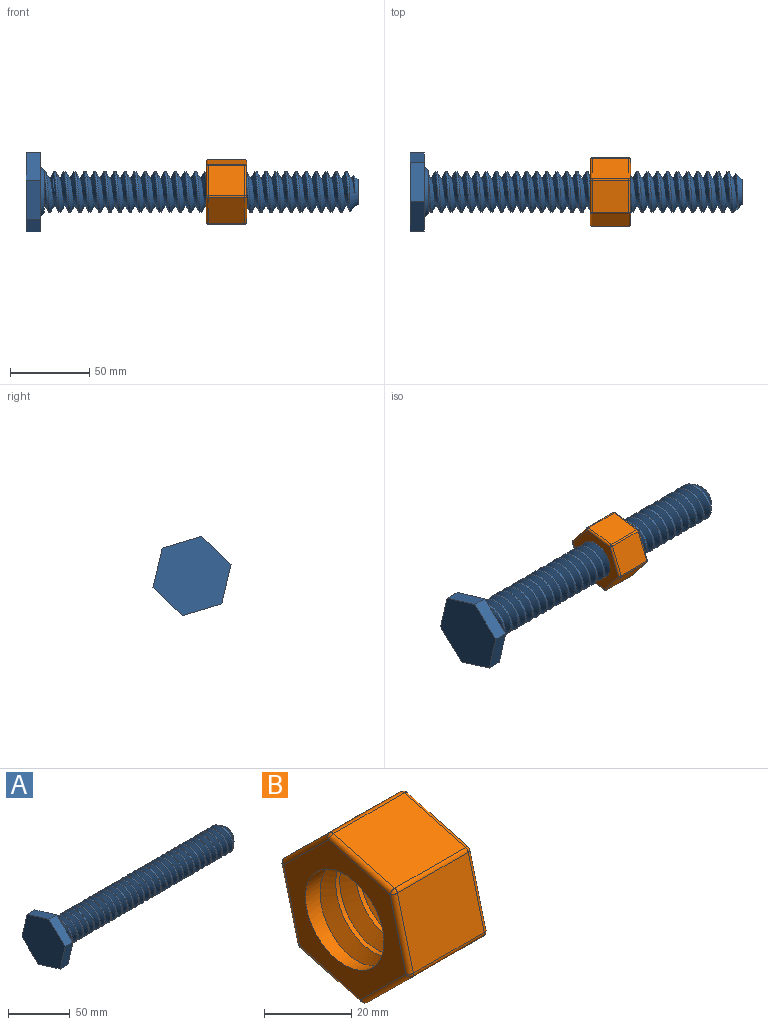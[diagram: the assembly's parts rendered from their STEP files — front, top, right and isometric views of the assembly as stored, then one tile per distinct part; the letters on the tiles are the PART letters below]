
ASSEMBLY  parts=2 mates=1
PART A: 16 faces, bbox 209.6x49.3x50.2 mm
  f0: plane 50.15x49.26mm, normal (1,0,0), area 936.9mm2, adj f1,f2,f3,f4,f5,f6,f15
  f1: plane 18.8x17.58mm, normal (0,-0.68,0.73), area 228.9mm2, adj f0,f2,f6,f7
  f2: plane 24.63x8.89mm, normal (0,0.29,0.96), area 228.9mm2, adj f0,f1,f3,f7
  f3: plane 25.08x8.89mm, normal (0,0.97,0.23), area 228.9mm2, adj f0,f2,f4,f7
  f4: plane 18.8x17.58mm, normal (0,0.68,-0.73), area 228.9mm2, adj f0,f3,f5,f7
  f5: plane 24.63x8.89mm, normal (0,-0.29,-0.96), area 228.9mm2, adj f0,f4,f6,f7
  f6: plane 25.08x8.89mm, normal (0,-0.97,-0.23), area 228.9mm2, adj f0,f1,f5,f7
  f7: plane 50.15x49.26mm, normal (-1,0,0), area 1721.8mm2, adj f1,f2,f3,f4,f5,f6
  f8: plane 26.53x26.53mm, normal (1,0,0), area 170.4mm2, adj f12,f13,f14,f15
  f9: plane 15.24x15.24mm, normal (1,0,0), area 182.4mm2, adj f10
  f10: cone r=7.62mm half-angle=45deg, axis (-1,0,0), area 325.5mm2, adj f9,f11,f12,f14
  f11: plane 4.4x3.22mm, normal (0,0,1), area 3mm2, adj f10,f12,f13
  f12: bspline ~201.51x29.33mm, area 10332.3mm2, adj f8,f10,f11,f13,f14
  f13: bspline ~198.33x29.33mm, area 10303.2mm2, adj f8,f11,f12,f14
  f14: cylinder r=12.7mm len=193.04mm, axis (-1,0,0), area 1188.4mm2, adj f8,f10,f12,f13
  f15: cone r=18.35mm half-angle=45deg, axis (-1,0,0), area 328.1mm2, adj f0,f8
PART B: 45 faces, bbox 31.7x44.8x45 mm
  f0: cylinder r=12.7mm len=25.4mm, axis (-1,0,0), area 455.9mm2, adj f1,f11,f12,f13,f14
  f1: cylinder r=12.7mm len=25.4mm, axis (-1,0,0), area 101.4mm2, adj f0,f2,f13,f14
  f2: cylinder r=12.7mm len=25.4mm, axis (-1,0,0), area 101.3mm2, adj f1,f3,f13,f14
  f3: cylinder r=12.7mm len=12.05mm, axis (-1,0,0), area 10.1mm2, adj f2,f10,f13,f14
  f4: plane 22.86x14.58mm, normal (0,0.7,0.71), area 468.5mm2, adj f33,f38,f41,f44
  f5: plane 22.86x19.76mm, normal (0,-0.26,0.96), area 468.5mm2, adj f30,f39,f40,f44
  f6: plane 22.86x19.83mm, normal (0,-0.97,0.25), area 468.5mm2, adj f20,f29,f30,f31
  f7: plane 22.86x14.58mm, normal (0,-0.7,-0.71), area 468.5mm2, adj f15,f19,f20,f21
  f8: plane 22.86x19.76mm, normal (0,0.26,-0.96), area 468.5mm2, adj f15,f18,f22,f23
  f9: plane 22.86x19.83mm, normal (0,0.97,-0.25), area 468.5mm2, adj f23,f28,f32,f33
  f10: plane 42.43x42.29mm, normal (1,0,0), area 427.6mm2, adj f3,f13,f14,f18,f19,f28,f29,f38
  f11: plane 39.65x39.52mm, normal (-1,0,0), area 584.3mm2, adj f0,f21,f22,f31,f32,f40,f41
  f12: plane 5.08x4.4mm, normal (0,0,-1), area 11.2mm2, adj f0,f13,f14
  f13: bspline ~39.49x34.2mm, area 1686.9mm2, adj f0,f1,f2,f3,f10,f12,f14
  f14: bspline ~39.49x34.2mm, area 1502.1mm2, adj f0,f1,f2,f3,f10,f12,f13
  f15: cylinder r=1.27mm len=22.86mm, axis (-1,0,0), area 30.4mm2, adj f7,f8,f16,f17
  f16: sphere r=1.27mm, area 1.7mm2, adj f15,f18,f19
  f17: sphere r=1.27mm, area 1.7mm2, adj f15,f21,f22
  f18: cylinder r=1.27mm len=20.1mm, axis (0,-0.96,-0.26), area 40.9mm2, adj f8,f10,f16,f24
  f19: cylinder r=1.27mm len=15.47mm, axis (0,-0.71,0.7), area 40.9mm2, adj f7,f10,f16,f25
  f20: cylinder r=1.27mm len=22.86mm, axis (-1,0,0), area 30.4mm2, adj f6,f7,f25,f26
  f21: cylinder r=1.27mm len=15.47mm, axis (0,0.71,-0.7), area 40.9mm2, adj f7,f11,f17,f26
  f22: cylinder r=1.27mm len=20.1mm, axis (0,0.96,0.26), area 40.9mm2, adj f8,f11,f17,f27
  f23: cylinder r=1.27mm len=22.86mm, axis (-1,0,0), area 30.4mm2, adj f8,f9,f24,f27
  f24: sphere r=1.27mm, area 1.1mm2, adj f18,f23,f28
  f25: sphere r=1.27mm, area 1.6mm2, adj f19,f20,f29
  f26: sphere r=1.27mm, area 1.3mm2, adj f20,f21,f31
  f27: sphere r=1.27mm, area 1.1mm2, adj f22,f23,f32
  f28: cylinder r=1.27mm len=20.15mm, axis (0,-0.25,-0.97), area 40.9mm2, adj f9,f10,f24,f34
  f29: cylinder r=1.27mm len=20.15mm, axis (0,0.25,0.97), area 40.9mm2, adj f6,f10,f25,f35
  f30: cylinder r=1.27mm len=22.86mm, axis (-1,0,0), area 30.4mm2, adj f5,f6,f35,f36
  f31: cylinder r=1.27mm len=20.15mm, axis (0,-0.25,-0.97), area 40.9mm2, adj f6,f11,f26,f36
  f32: cylinder r=1.27mm len=20.15mm, axis (0,0.25,0.97), area 40.9mm2, adj f9,f11,f27,f37
  f33: cylinder r=1.27mm len=22.86mm, axis (-1,0,0), area 30.4mm2, adj f4,f9,f34,f37
  f34: sphere r=1.27mm, area 1.3mm2, adj f28,f33,f38
  f35: sphere r=1.27mm, area 1mm2, adj f29,f30,f39
  f36: sphere r=1.27mm, area 1.1mm2, adj f30,f31,f40
  f37: sphere r=1.27mm, area 1.3mm2, adj f32,f33,f41
  f38: cylinder r=1.27mm len=15.47mm, axis (0,0.71,-0.7), area 40.9mm2, adj f4,f10,f34,f42
  f39: cylinder r=1.27mm len=20.1mm, axis (0,0.96,0.26), area 40.9mm2, adj f5,f10,f35,f42
  f40: cylinder r=1.27mm len=20.1mm, axis (0,-0.96,-0.26), area 40.9mm2, adj f5,f11,f36,f43
  f41: cylinder r=1.27mm len=15.47mm, axis (0,-0.71,0.7), area 40.9mm2, adj f4,f11,f37,f43
  f42: sphere r=1.27mm, area 1.7mm2, adj f38,f39,f44
  f43: sphere r=1.27mm, area 1.7mm2, adj f40,f41,f44
  f44: cylinder r=1.27mm len=22.86mm, axis (-1,0,0), area 30.4mm2, adj f4,f5,f42,f43
PLACE A t=(-88.65,-67.58,32.75)mm fixed
PLACE B rot(axis=(1,0,0),172.7deg) t=(-82.81,-67.58,32.75)mm
MATE cylindrical A.f10 <-> B.f0  axis (1,0,0) through (12.95,-67.58,32.75)mm
